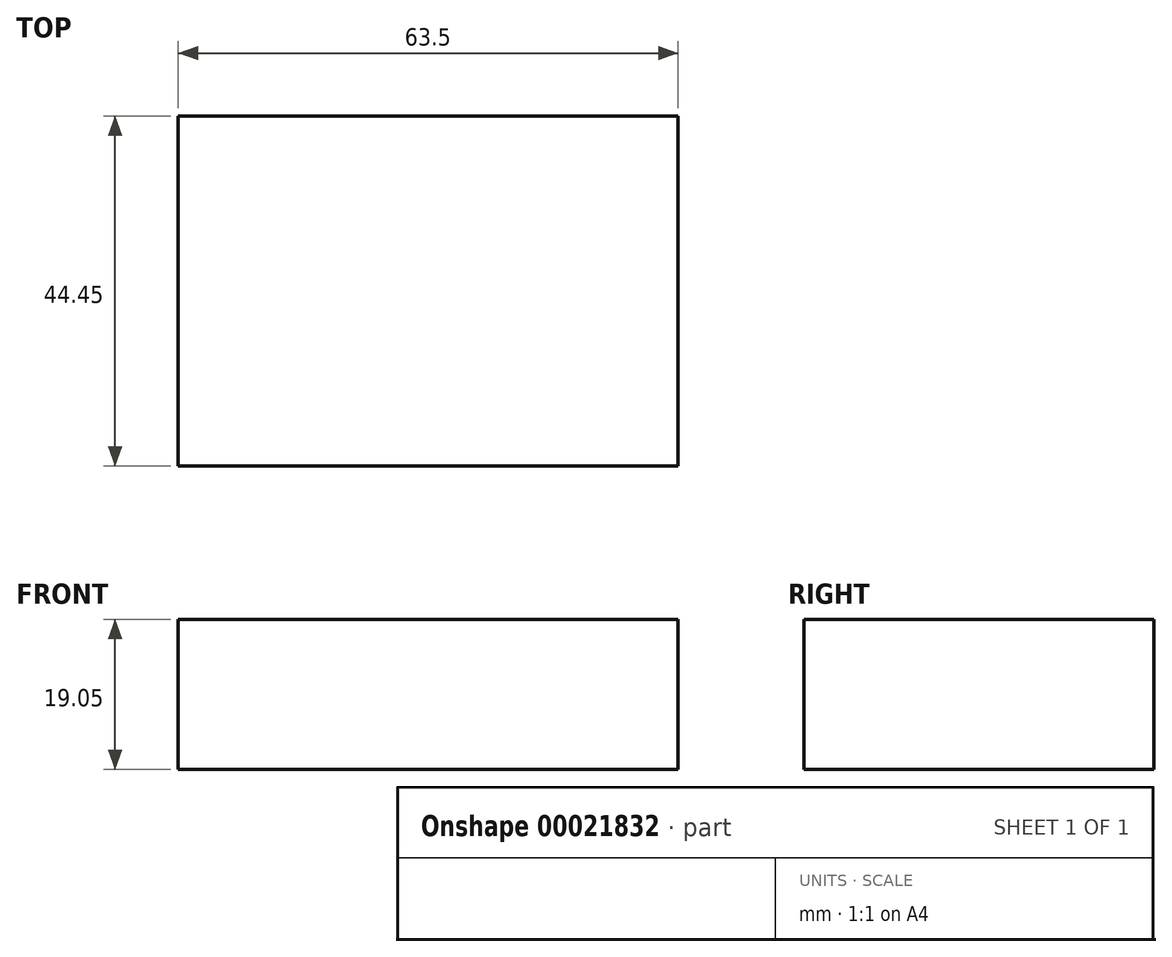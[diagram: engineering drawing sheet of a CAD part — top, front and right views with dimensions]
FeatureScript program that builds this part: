
annotation { "Feature Type Name" : "Feature", "Feature Type Description" : "" }
export const myFeature = defineFeature(function(context is Context, id is Id, definition is map)
    precondition{}
    {
        {
            var Q0;
            Q0=qCreatedBy(makeId("Top.planeOp"),FACE);
            var sketch = newSketch(context, id + "F0", { "sketchPlane" : qUnion([Q0])});
            skLineSegment(sketch, "E0.bottom", {"start": v(-23.35, 29.55) * mm, "end": v(40.15, 29.55) * mm});
            skLineSegment(sketch, "E0.top", {"start": v(-23.35, -14.9) * mm, "end": v(40.15, -14.9) * mm});
            skLineSegment(sketch, "E0.left", {"start": v(-23.35, 29.55) * mm, "end": v(-23.35, -14.9) * mm});
            skLineSegment(sketch, "E0.right", {"start": v(40.15, 29.55) * mm, "end": v(40.15, -14.9) * mm});
            skSolve(sketch);
        }
        {
            var Q0;
            Q0 = qSketchRegion(id + "F0", true);
            extrude(context, id + "F1", {"entities" : qUnion([Q0]), "depth" : 19.05 * mm});
        }
    });
